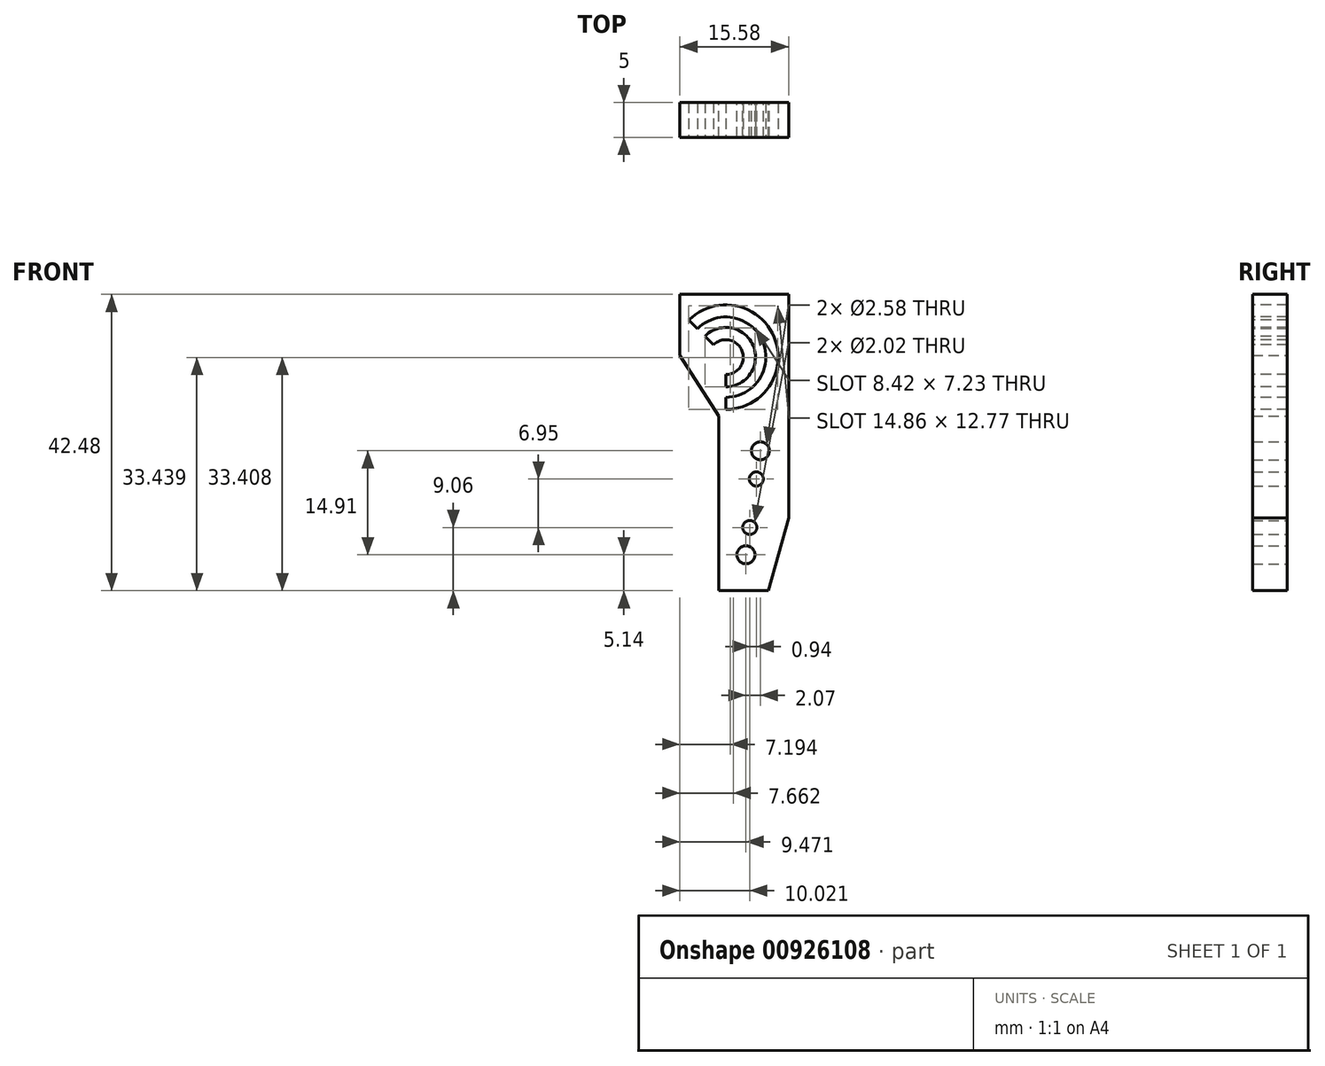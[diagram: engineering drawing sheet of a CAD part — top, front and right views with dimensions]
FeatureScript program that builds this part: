
annotation { "Feature Type Name" : "Feature", "Feature Type Description" : "" }
export const myFeature = defineFeature(function(context is Context, id is Id, definition is map)
    precondition{}
    {
        {
            var Q0;
            Q0=qCreatedBy(makeId("Front.planeOp"),FACE);
            var sketch = newSketch(context, id + "F0", { "sketchPlane" : qUnion([Q0])});
            skLineSegment(sketch, "E0", {"start": v(-37.2, 26.47) * mm, "end": v(-21.63, 26.47) * mm});
            skLineSegment(sketch, "E1", {"start": v(-31.6, -16.01) * mm, "end": v(-24.5, -16.01) * mm});
            skLineSegment(sketch, "E2", {"start": v(-21.63, 26.47) * mm, "end": v(-21.63, -5.57) * mm});
            skLineSegment(sketch, "E3", {"start": v(-21.63, -5.57) * mm, "end": v(-24.5, -16.01) * mm});
            skCircle(sketch, "E4", {"center": v(-26.25, 0) * mm, "radius": 1.01 * mm});
            skCircle(sketch, "E5", {"center": v(-25.67, 4.04) * mm, "radius": 1.29 * mm});
            skLineSegment(sketch, "E6", {"start": v(-37.2, 26.47) * mm, "end": v(-37.2, 17.75) * mm});
            skLineSegment(sketch, "E7", {"start": v(-31.6, 9.02) * mm, "end": v(-37.2, 17.75) * mm});
            skCircle(sketch, "E8", {"center": v(-27.74, -10.87) * mm, "radius": 1.29 * mm});
            skLineSegment(sketch, "E9", {"start": v(-31.6, 9.02) * mm, "end": v(-31.6, -16.01) * mm});
            skCircle(sketch, "E10", {"center": v(-27.19, -6.95) * mm, "radius": 1.01 * mm});
            skSolve(sketch);
        }
        {
            var Q0;
            Q0 = qSketchRegion(id + "F0", true);
            extrude(context, id + "F1", {"entities" : qUnion([Q0]), "depth" : 5 * mm, "offsetDistance" : 25 * mm});
        }
        {
            var Q0;
            Q0=makeQuery(id+"F1.opExtrude","CAP_FACE",FACE,{"disambiguationData":[OSD([sQuery(id+"F0.wireOp",EDGE,"E0"),sQuery(id+"F0.wireOp",EDGE,"vhafAufr-sMwy-97n5-iXBO-xDqB0n5jxu3E"),sQuery(id+"F0.wireOp",EDGE,"UXBwDhYX-UGdj-3Fuf-0lg6-L2S2GxCH4KdO"),sQuery(id+"F0.wireOp",EDGE,"E1"),sQuery(id+"F0.wireOp",EDGE,"E2"),sQuery(id+"F0.wireOp",EDGE,"E3"),sQuery(id+"F0.wireOp",EDGE,"Bw1zWa2v-cGN4-3EgK-JfqL-teRUB2vv49dp"),sQuery(id+"F0.wireOp",EDGE,"ZTFXdPh2-o7Oq-T5VS-Xypz-DnaIlgl5ERol"),sQuery(id+"F0.wireOp",EDGE,"QQ8wmM1o-sOxR-a1Cs-1UE6-A4rnuhCYcdFK"),sQuery(id+"F0.wireOp",EDGE,"E4"),sQuery(id+"F0.wireOp",EDGE,"E5")])],"isStart":false});
            var sketch = newSketch(context, id + "F2", { "sketchPlane" : qUnion([Q0])});
            skArc(sketch, "E11", {"start": v(-30.63, 14.97) * mm, "mid": v(-28.32, 18.43) * mm, "end": v(-32.4, 19.24) * mm});
            skArc(sketch, "E12", {"start": v(-30.63, 13.22) * mm, "mid": v(-26.7, 19.1) * mm, "end": v(-33.63, 20.48) * mm});
            skArc(sketch, "E13", {"start": v(-30.63, 11.72) * mm, "mid": v(-25.32, 19.67) * mm, "end": v(-34.7, 21.54) * mm});
            skArc(sketch, "E14", {"start": v(-30.63, 9.97) * mm, "mid": v(-23.7, 20.34) * mm, "end": v(-35.93, 22.77) * mm});
            skLineSegment(sketch, "E15", {"start": v(-30.63, 14.97) * mm, "end": v(-30.63, 13.22) * mm});
            skLineSegment(sketch, "E16", {"start": v(-32.4, 19.24) * mm, "end": v(-33.63, 20.48) * mm});
            skLineSegment(sketch, "E17.trimOffspring", {"start": v(-34.7, 21.54) * mm, "end": v(-35.93, 22.77) * mm});
            skLineSegment(sketch, "E18.trimOffspring", {"start": v(-30.63, 11.72) * mm, "end": v(-30.63, 9.97) * mm});
            skSolve(sketch);
        }
        {
            var Q0;
            Q0 = qSketchRegion(id + "F2", true);
            extrude(context, id + "F3", {"entities" : qUnion([Q0]), "operationType" : NewBodyOperationType.REMOVE, "endBound" : BoundingType.THROUGH_ALL, "oppositeDirection" : true, "depth" : 25 * mm, "offsetDistance" : 25 * mm});
        }
    });
